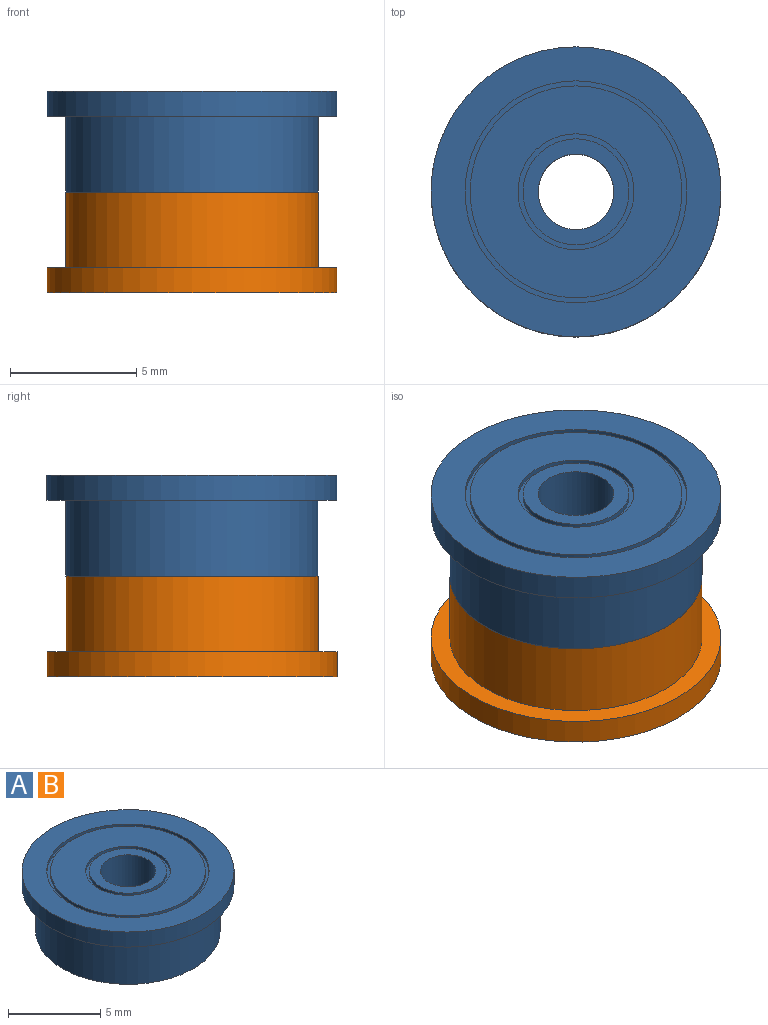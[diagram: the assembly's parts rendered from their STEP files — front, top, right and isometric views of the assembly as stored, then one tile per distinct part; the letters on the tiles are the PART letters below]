
ASSEMBLY  parts=2 mates=1
PART A: 22 faces, bbox 11.5x11.5x4 mm
  f0: cylinder r=5mm len=10mm, axis (0,0,-1), area 94.2mm2, adj f20,f21
  f1: cylinder r=4.4mm len=8.8mm, axis (0,0,-1), area 5.5mm2, adj f19,f21
  f2: cylinder r=5.75mm len=11.5mm, axis (0,0,-1), area 36.1mm2, adj f18,f20
  f3: cylinder r=4.2mm len=8.4mm, axis (0,0,-1), area 5.3mm2, adj f17,f19
  f4: cylinder r=4.4mm len=8.8mm, axis (0,0,-1), area 5.5mm2, adj f16,f18
  f5: cylinder r=2.3mm len=4.6mm, axis (0,0,-1), area 2.9mm2, adj f15,f17
  f6: cylinder r=4.2mm len=8.4mm, axis (0,0,-1), area 5.3mm2, adj f14,f16
  f7: cylinder r=2.1mm len=4.2mm, axis (0,0,-1), area 2.6mm2, adj f13,f15
  f8: cylinder r=2.3mm len=4.6mm, axis (0,0,-1), area 2.9mm2, adj f12,f14
  f9: cylinder r=1.5mm len=4mm, axis (0,0,1), area 37.7mm2, adj f11,f13
  f10: cylinder r=2.1mm len=4.2mm, axis (0,0,-1), area 2.6mm2, adj f11,f12
  f11: plane 4.2x4.2mm, normal (0,0,1), area 6.8mm2, adj f9,f10
  f12: plane 4.6x4.6mm, normal (0,0,1), area 2.8mm2, adj f8,f10
  f13: plane 4.2x4.2mm, normal (0,0,-1), area 6.8mm2, adj f7,f9
  f14: plane 8.4x8.4mm, normal (0,0,1), area 38.8mm2, adj f6,f8
  f15: plane 4.6x4.6mm, normal (0,0,-1), area 2.8mm2, adj f5,f7
  f16: plane 8.8x8.8mm, normal (0,0,1), area 5.4mm2, adj f4,f6
  f17: plane 8.4x8.4mm, normal (0,0,-1), area 38.8mm2, adj f3,f5
  f18: plane 11.5x11.5mm, normal (0,0,1), area 43mm2, adj f2,f4
  f19: plane 8.8x8.8mm, normal (0,0,-1), area 5.4mm2, adj f1,f3
  f20: plane 11.5x11.5mm, normal (0,0,-1), area 25.3mm2, adj f0,f2
  f21: plane 10x10mm, normal (0,0,-1), area 17.7mm2, adj f0,f1
PART B: same geometry as A
PLACE A t=(-0.08,-0.17,-0.08)mm
PLACE B rot(axis=(1,0,0),180deg) t=(-0.08,-0.17,-0.08)mm
MATE fastened B.f0 <-> A.f0  axis (0,0,1) through (-0.08,-0.17,-0.08)mm
